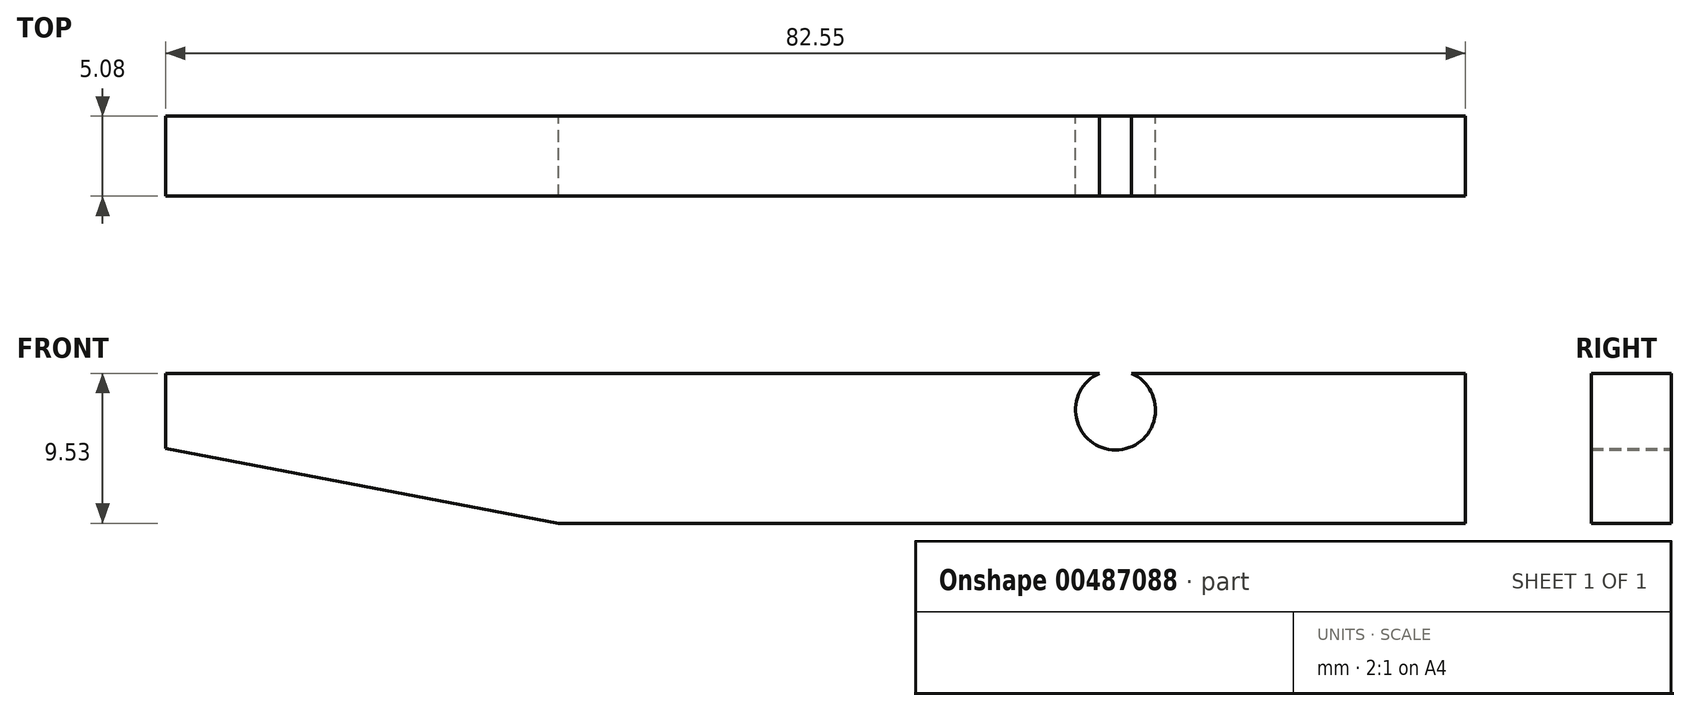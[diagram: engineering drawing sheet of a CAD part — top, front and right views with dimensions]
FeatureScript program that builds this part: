
annotation { "Feature Type Name" : "Feature", "Feature Type Description" : "" }
export const myFeature = defineFeature(function(context is Context, id is Id, definition is map)
    precondition{}
    {
        {
            var Q0;
            Q0=qCreatedBy(makeId("Front.planeOp"),FACE);
            var sketch = newSketch(context, id + "F0", { "sketchPlane" : qUnion([Q0])});
            skLineSegment(sketch, "E0.bottom", {"start": v(-51.24, -8.1) * mm, "end": v(8.07, -8.1) * mm});
            skLineSegment(sketch, "E0.top", {"start": v(-26.29, -17.63) * mm, "end": v(31.31, -17.63) * mm});
            skLineSegment(sketch, "E0.left", {"start": v(-51.24, -8.1) * mm, "end": v(-51.24, -12.87) * mm});
            skLineSegment(sketch, "E0.right", {"start": v(31.31, -8.1) * mm, "end": v(31.31, -17.63) * mm});
            skLineSegment(sketch, "E1", {"start": v(9.09, 0) * mm, "end": v(9.09, -8.1) * mm});
            skLineSegment(sketch, "E2", {"start": v(31.31, -8.1) * mm, "end": v(31.31, 0) * mm});
            skArc(sketch, "E3", {"start": v(8.07, -8.1) * mm, "mid": v(9.09, -12.98) * mm, "end": v(10.1, -8.1) * mm});
            skLineSegment(sketch, "E4.trimOffspring", {"start": v(10.1, -8.1) * mm, "end": v(31.31, -8.1) * mm});
            skLineSegment(sketch, "E5", {"start": v(-51.24, -12.87) * mm, "end": v(-26.29, -17.63) * mm});
            skPoint(sketch, "E6.orphan", {"position": v(-51.24, -17.63) * mm});
            skSolve(sketch);
        }
        {
            var Q0;
            Q0 = qSketchRegion(id + "F0", true);
            extrude(context, id + "F1", {"entities" : qUnion([Q0]), "depth" : 5.08 * mm});
        }
    });
